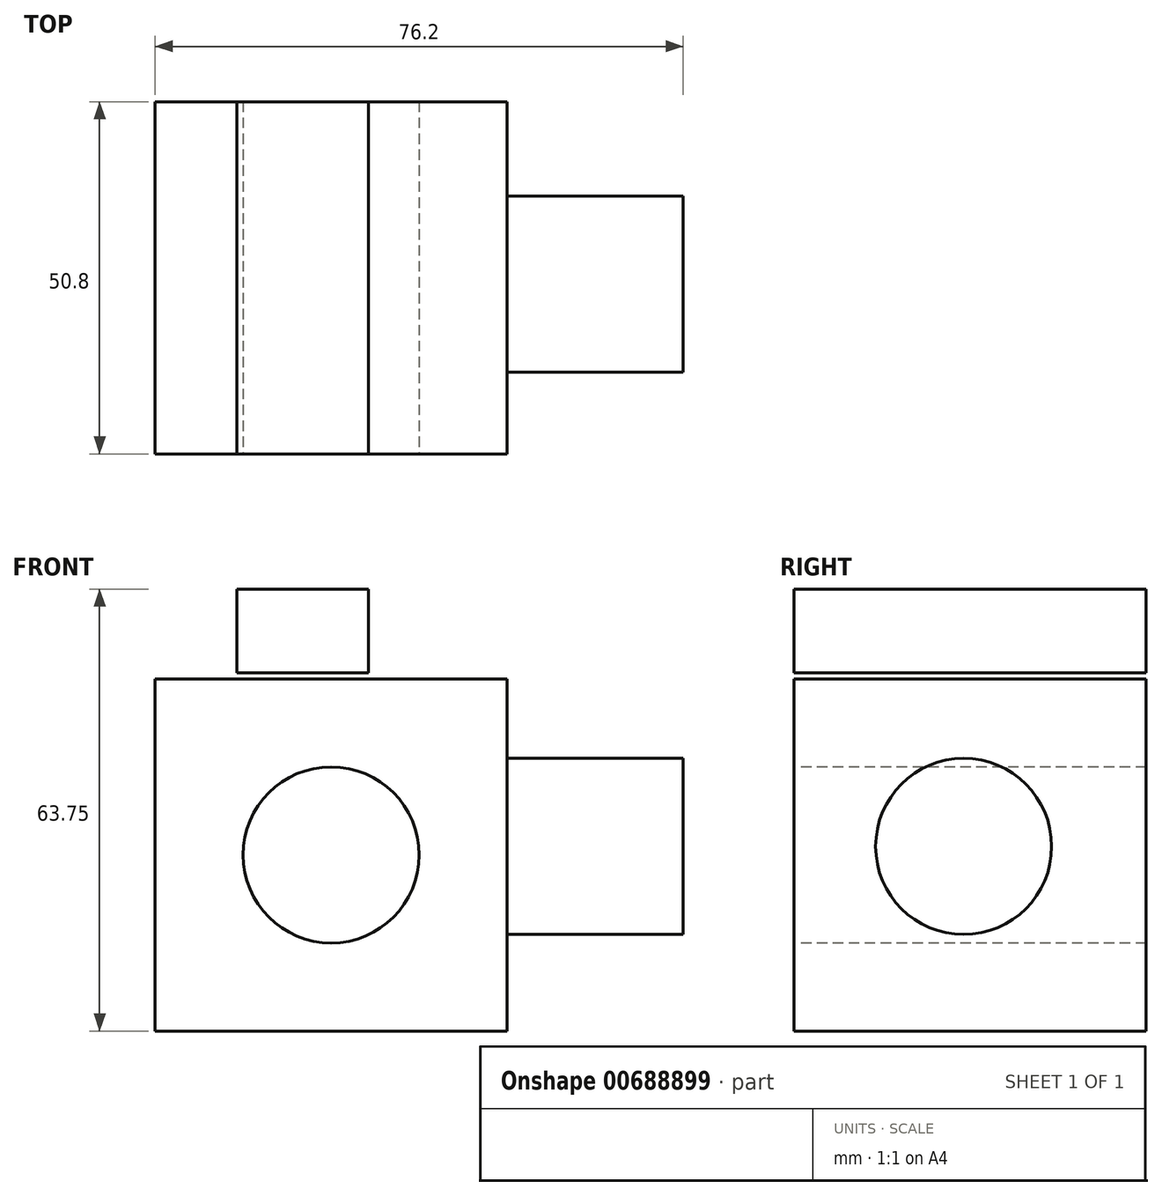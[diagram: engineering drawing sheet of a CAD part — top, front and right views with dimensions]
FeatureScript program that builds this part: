
annotation { "Feature Type Name" : "Feature", "Feature Type Description" : "" }
export const myFeature = defineFeature(function(context is Context, id is Id, definition is map)
    precondition{}
    {
        {
            var Q0;
            Q0=qCreatedBy(makeId("Front.planeOp"),FACE);
            var sketch = newSketch(context, id + "F0", { "sketchPlane" : qUnion([Q0])});
            skLineSegment(sketch, "E0.bottom", {"start": v(0, 0) * mm, "end": v(-50.8, 0) * mm});
            skLineSegment(sketch, "E0.top", {"start": v(0, 50.8) * mm, "end": v(-50.8, 50.8) * mm});
            skLineSegment(sketch, "E0.left", {"start": v(0, 0) * mm, "end": v(0, 50.8) * mm});
            skLineSegment(sketch, "E0.right", {"start": v(-50.8, 0) * mm, "end": v(-50.8, 50.8) * mm});
            skSolve(sketch);
        }
        {
            var Q0;
            Q0 = qSketchRegion(id + "F0", true);
            extrude(context, id + "F1", {"entities" : qUnion([Q0]), "depth" : 50.8 * mm, "offsetDistance" : 25.4 * mm});
        }
        {
            var Q0;
            Q0=makeQuery(id+"F1.opExtrude","CAP_FACE",FACE,{"disambiguationData":[OSD([sQuery(id+"F0.wireOp",EDGE,"E0.bottom"),sQuery(id+"F0.wireOp",EDGE,"E0.top"),sQuery(id+"F0.wireOp",EDGE,"E0.left"),sQuery(id+"F0.wireOp",EDGE,"E0.right")])],"isStart":false});
            var sketch = newSketch(context, id + "F2", { "sketchPlane" : qUnion([Q0])});
            skCircle(sketch, "E1", {"center": v(-25.4, 25.4) * mm, "radius": 12.7 * mm});
            skSolve(sketch);
        }
        {
            var Q0;
            Q0=makeQuery(id+"F2.imprint","IMPRINT",FACE,{"disambiguationData":[TD([[makeQuery(id+"F2.imprint","IMPRINT",EDGE,{"derivedFrom":sQuery(id+"F2.wireOp",EDGE,"E1")}),1.0]])]});
            extrude(context, id + "F3", {"entities" : qUnion([Q0]), "operationType" : NewBodyOperationType.REMOVE, "oppositeDirection" : true, "depth" : 50.8 * mm, "offsetDistance" : 25.4 * mm});
        }
        {
            var Q0;
            Q0=qCreatedBy(makeId("Front.planeOp"),FACE);
            var sketch = newSketch(context, id + "F4", { "sketchPlane" : qUnion([Q0])});
            skLineSegment(sketch, "E2.bottom", {"start": v(-20, 51.66) * mm, "end": v(-39, 51.66) * mm});
            skLineSegment(sketch, "E2.top", {"start": v(-20, 63.75) * mm, "end": v(-39, 63.75) * mm});
            skLineSegment(sketch, "E2.left", {"start": v(-20, 51.66) * mm, "end": v(-20, 63.75) * mm});
            skLineSegment(sketch, "E2.right", {"start": v(-39, 51.66) * mm, "end": v(-39, 63.75) * mm});
            skSolve(sketch);
        }
        {
            var Q0;
            Q0 = qSketchRegion(id + "F4", true);
            extrude(context, id + "F5", {"entities" : qUnion([Q0]), "depth" : 50.8 * mm, "offsetDistance" : 25.4 * mm});
        }
        {
            var Q0;
            Q0=qCreatedBy(makeId("Right.planeOp"),FACE);
            var sketch = newSketch(context, id + "F6", { "sketchPlane" : qUnion([Q0])});
            skCircle(sketch, "E3", {"center": v(-26.33, 26.62) * mm, "radius": 12.7 * mm});
            skSolve(sketch);
        }
        {
            var Q0;
            Q0 = qSketchRegion(id + "F6", true);
            extrude(context, id + "F7", {"entities" : qUnion([Q0]), "operationType" : NewBodyOperationType.ADD, "depth" : 25.4 * mm, "offsetDistance" : 25.4 * mm});
        }
    });
